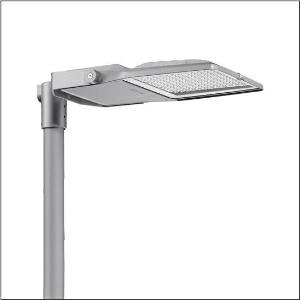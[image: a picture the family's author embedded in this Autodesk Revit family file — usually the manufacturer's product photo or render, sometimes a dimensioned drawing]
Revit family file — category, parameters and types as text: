
# Revit family: floodlight_fl_21_iq_midi___pl33t_5xa7782f4f3a_5715
name_source: partatom
category: Lighting Fixtures
units: mm (PartAtom-declared; Revit-internal decimal feet)

## family parameters
Cut with Voids When Loaded = No
Host = Face
Light Source = No
Part Type = Normal
Room Calculation Point = No
Round Connector Dimension = Use Diameter
Shared = No

## types (1)
- --- (1 x LED, 36900 lm, 270.2 W, 4000K)
    Apparent Load = 270 VA
    CIE Flux Codes = 26 75 99 100 100
    Color Rendering = 70
    Color Temperature = 4000K
    Default Elevation = 1800 mm
    Description = Floodlight FL 21 iQ midi, floodlight, primary light control with lens, of PMMA, primary optical cover: protective disc, of toughened safety glass, transparent, light distribution: PL33T, light emission: direct distribution, installation type: surface-mounted, LED, High Power LED, rated luminous flux: 36.900lm, luminous efficacy: 137lm/W, light colour: 740, colour temperature: 4000K, control gear: ECG iQ, control: optimised constant luminous flux control (CLO 2.0), Desk-Remote (wireless, voltage-free reading and setting of iQ features in the workshop via application-optimized NFC function/RFID function), Smart-Wire, Night-Set, Temp-Guard, Auto-Match, Street-Remote, with terminal, 6-pole, mains connection: 220..240V, AC, 50/60Hz, start of lifetime: 270W, end of service life: 287W, reduction: 118W, luminaire housing, of diecast aluminium, powder-coated, Siteco® metallic grey (DB 702S), corrosivity category C5 mid according to DIN EN ISO 12944, sealing non-destructively replaceable, please order mast flange separately, mast bracket, of steel, galvanised, powder-coated, Siteco® metallic grey (DB 702S), protection rating (complete): IP66, insulation class (complete): insulation class II (safety insulation), certification: CE, protection symbol: D, impact resistance: IK08, permissible operating ambient temperature: -40..+40°C, permissible operating ambient temperature for outdoor applications: -40..+50°C, standard: DIN EN 12944, LABS conformity tested according to VDMA 24364:2018-05, packaging unit: 1 piece

Light Distribution: PL33T
    Height = 76 mm
    Lamp = 1 x LED
    Lamp Light Flux = 36900 lm
    Lamp Power = 270.2 W
    Lamp count = 1
    Length = 657 mm
    Luminous efficacy = 137 lm/W
    Manufacturer = Siteco
    ModVariant = No
    Model = 5XA7782F4F3A
    Number of Poles = 1
    OnlyDefault = Yes
    Power Factor = 1
    Product Name = Floodlight FL 21 iQ midi | PL33T
    Product group = floodlight | pylon annexe
    ProductGroupID = 6200
    Protection Class = Protection class II
    Protection Degree = IP 66
    RLX_Detail_Level = 1
    RLX_Emergency_Light_Flux = 0 lm
    RLX_Emergency_Type = 0
    RLX_Emergency_Type_DB = No
    RlxData = <blob elided: 153653 chars, md5=e44d0c4b>
    Socket = socket
    Standby Power = 0 W
    System Light Flux = 36900 lm
    System Power = 270 W
    Type Comments = factory setting: luminous flux: 100 % | dim-lin: 254 | 620 mA
    Type Image = l_1007123.jpg
    URL = http://relux.com
    VarID = @adj_051545
    Voltage = 0 V
    Weight = 0.00 kg
    Width = 442 mm

## geometry (parser evidence)
native form markers: Blend x4, Sweep x12
no freeform markers — native parametric forms only
